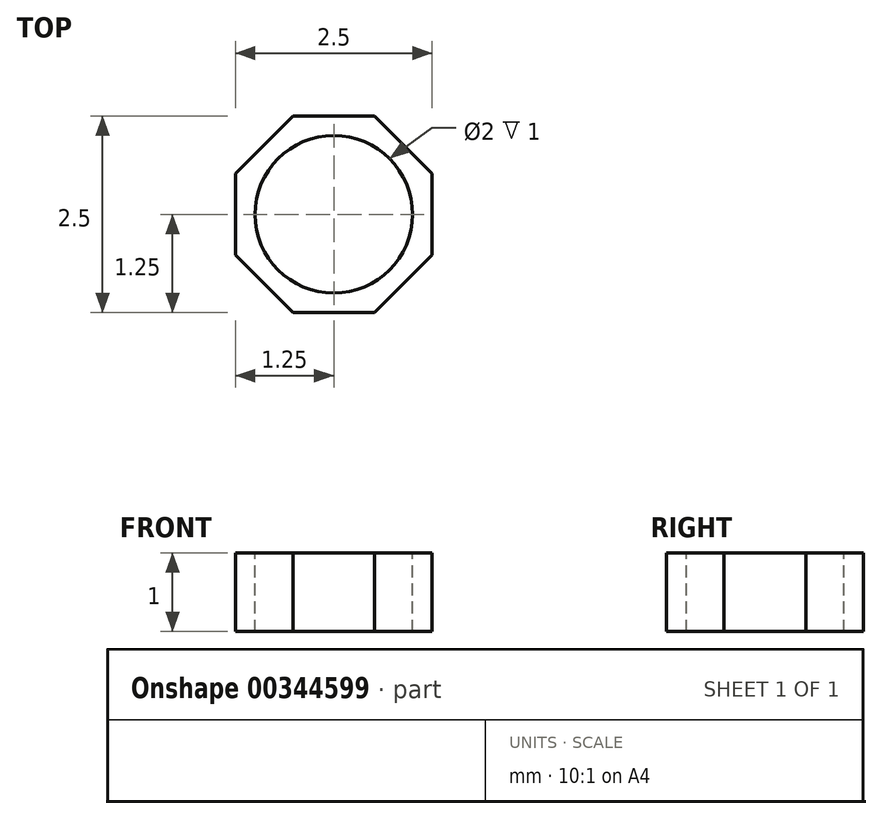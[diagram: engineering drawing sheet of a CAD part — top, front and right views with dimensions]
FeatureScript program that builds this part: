
annotation { "Feature Type Name" : "Feature", "Feature Type Description" : "" }
export const myFeature = defineFeature(function(context is Context, id is Id, definition is map)
    precondition{}
    {
        {
            var Q0;
            Q0=qCreatedBy(makeId("Top.planeOp"),FACE);
            var sketch = newSketch(context, id + "F0", { "sketchPlane" : qUnion([Q0])});
            skLineSegment(sketch, "E0", {"start": v(0, 0) * mm, "end": v(0, 1.25) * mm});
            skLineSegment(sketch, "E1", {"start": v(0, 0) * mm, "end": v(0, -1.25) * mm});
            skLineSegment(sketch, "E2", {"start": v(0, 0) * mm, "end": v(1.25, 0) * mm});
            skLineSegment(sketch, "E3", {"start": v(0, 0) * mm, "end": v(-1.25, 0) * mm});
            skLineSegment(sketch, "E4", {"start": v(-1.25, 0) * mm, "end": v(-1.25, -0.52) * mm});
            skLineSegment(sketch, "E5", {"start": v(-1.25, -0.52) * mm, "end": v(-1.25, 0.52) * mm});
            skLineSegment(sketch, "E6.bottom", {"start": v(-0.52, 1.25) * mm, "end": v(0.52, 1.25) * mm});
            skLineSegment(sketch, "E6.top", {"start": v(-0.52, -1.25) * mm, "end": v(0.52, -1.25) * mm});
            skLineSegment(sketch, "E6.left", {"start": v(-1.25, 0.52) * mm, "end": v(-1.25, -0.52) * mm});
            skLineSegment(sketch, "E6.right", {"start": v(1.25, 0.52) * mm, "end": v(1.25, -0.52) * mm});
            skLineSegment(sketch, "E7", {"start": v(0, 0) * mm, "end": v(0.89, 0.88) * mm});
            skLineSegment(sketch, "E8", {"start": v(0, 0) * mm, "end": v(-0.89, -0.88) * mm});
            skLineSegment(sketch, "E9", {"start": v(0, 0) * mm, "end": v(0.88, -0.89) * mm});
            skLineSegment(sketch, "E10", {"start": v(0, 0) * mm, "end": v(-0.88, 0.89) * mm});
            skLineSegment(sketch, "E11", {"start": v(-0.88, 0.89) * mm, "end": v(-1.25, 0.52) * mm});
            skLineSegment(sketch, "E12", {"start": v(-1.25, 0.52) * mm, "end": v(-0.52, 1.25) * mm});
            skLineSegment(sketch, "E13.bottom", {"start": v(0.52, 1.25) * mm, "end": v(1.25, 0.52) * mm});
            skLineSegment(sketch, "E13.top", {"start": v(-1.25, -0.52) * mm, "end": v(-0.52, -1.25) * mm});
            skLineSegment(sketch, "E13.left", {"start": v(-0.52, 1.25) * mm, "end": v(-1.25, 0.52) * mm});
            skLineSegment(sketch, "E13.right", {"start": v(1.25, -0.52) * mm, "end": v(0.52, -1.25) * mm});
            skLineSegment(sketch, "E14.0", {"start": v(-0.89, -0.88) * mm, "end": v(-0.52, -1.25) * mm, "construction": true});
            skLineSegment(sketch, "E15.0", {"start": v(0.52, -1.25) * mm, "end": v(0.88, -0.89) * mm, "construction": true});
            skSolve(sketch);
        }
        {
            var Q0;
            Q0 = qSketchRegion(id + "F0", true);
            extrude(context, id + "F1", {"entities" : qUnion([Q0]), "depth" : 1 * mm});
        }
        {
            var Q0;
            Q0=makeQuery(id+"F1.opExtrude","CAP_FACE",FACE,{"disambiguationData":[OSD([sQuery(id+"F0.wireOp",EDGE,"E6.bottom"),sQuery(id+"F0.wireOp",EDGE,"E6.top"),sQuery(id+"F0.wireOp",EDGE,"E6.left"),sQuery(id+"F0.wireOp",EDGE,"E6.right"),sQuery(id+"F0.wireOp",EDGE,"E13.bottom"),sQuery(id+"F0.wireOp",EDGE,"E13.top"),sQuery(id+"F0.wireOp",EDGE,"E13.left"),sQuery(id+"F0.wireOp",EDGE,"E13.right")])],"isStart":false});
            var sketch = newSketch(context, id + "F2", { "sketchPlane" : qUnion([Q0])});
            skCircle(sketch, "E16", {"center": v(0, 0) * mm, "radius": 1 * mm});
            skSolve(sketch);
        }
        {
            var Q0;
            Q0 = qSketchRegion(id + "F2", true);
            extrude(context, id + "F3", {"entities" : qUnion([Q0]), "operationType" : NewBodyOperationType.REMOVE, "oppositeDirection" : true, "depth" : 25 * mm});
        }
    });
